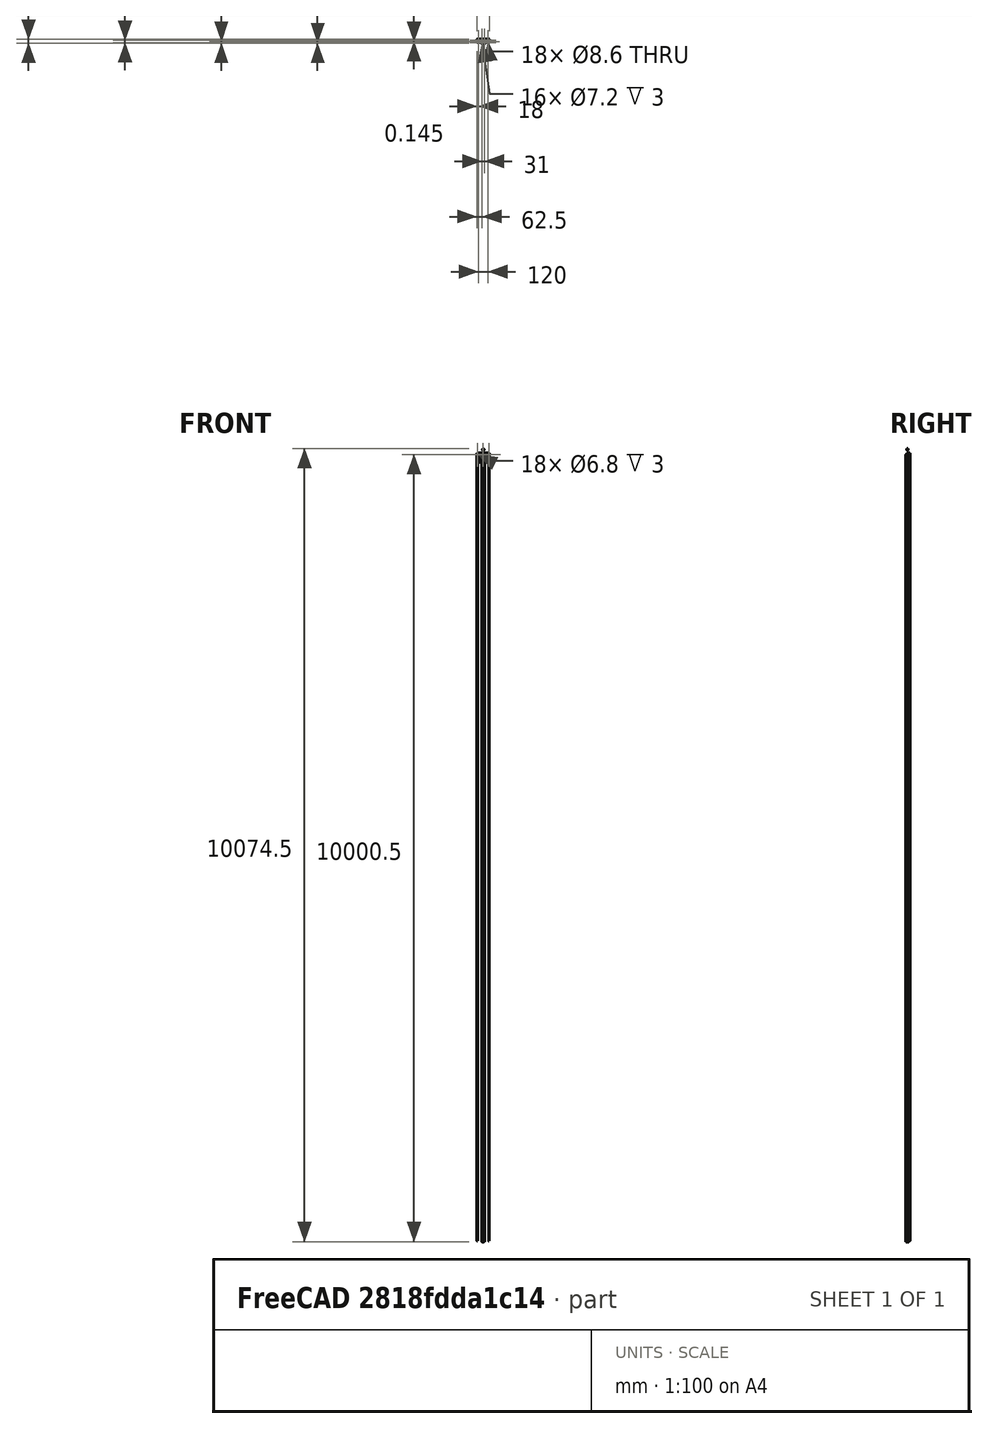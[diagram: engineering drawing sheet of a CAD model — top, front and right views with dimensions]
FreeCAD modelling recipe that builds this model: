
FCSTD DOCUMENT  (FreeCAD 0.15R4671 (Git))
Label: ZRodHolderMiddle
License: All rights reserved
LicenseURL: http://en.wikipedia.org/wiki/All_rights_reserved
objects: Sketcher::SketchObject×13, PartDesign::Pocket×10, PartDesign::Fillet×7, Part::Feature×4, PartDesign::Pad×3, PartDesign::Chamfer×2, Mesh::Feature×2
note: 52 computed .brp shape members not serialized (recipe doc carries the construction recipe); baked Part::Feature solids carry a one-line shape summary decoded from their .brp

FEATURE [Part::Feature] Part__Feature  label="TempZMotorEnd"
  shape: bbox 155 x 49.5 x 115 mm, 106 faces (baked)
FEATURE [Part::Feature] _mmBrasNut  label="8mmBrassNut"
  Placement = pos=(0,-28.14,59) rot=(0.707107,0,0.707107;3.14159rad)
  shape: bbox 22 x 22 x 16.42 mm, 29 faces (baked)
FEATURE [Sketcher::SketchObject] Sketch
  Placement = pos=(0,0,0) rot=(1,0,0;1.5708rad)
  sketch-geometry (4):
    g0: LineSegment StartX=-78 StartY=7.5 StartZ=0 EndX=78 EndY=7.5 EndZ=0
    g1: LineSegment StartX=78 StartY=7.5 StartZ=0 EndX=78 EndY=-7.5 EndZ=0
    g2: LineSegment StartX=78 StartY=-7.5 StartZ=0 EndX=-78 EndY=-7.5 EndZ=0
    g3: LineSegment StartX=-78 StartY=-7.5 StartZ=0 EndX=-78 EndY=7.5 EndZ=0
  constraints (12):
    c: Coincident(g0,g1)
    c: Coincident(g1,g2)
    c: Coincident(g2,g3)
    c: Coincident(g3,g0)
    c: Horizontal(g0)
    c: Horizontal(g2)
    c: Vertical(g1)
    c: Vertical(g3)
    c: DistanceY(g1,g0) = 15
    c: DistanceY(g-1,g1) = -7.5
    c: DistanceX(g1,g2) = -156
    c: DistanceX(g-1,g2) = -78
FEATURE [PartDesign::Pad] Pad
  Length = 36
  Length2 = 100
  Placement = pos=(0,0,0) rot=(1,0,0;1.5708rad)
  Sketch = -> Sketch
  Type = 0
FEATURE [Sketcher::SketchObject] Sketch001
  Placement = pos=(0,0,7.5) rot=(0,0,1;3.14159rad)
  Support = -> Pad [Face1]
  sketch-geometry (16):
    g0: LineSegment StartX=-80 StartY=7 StartZ=0 EndX=-68 EndY=7 EndZ=0
    g1: LineSegment StartX=-68 StartY=7 StartZ=0 EndX=-68 EndY=37 EndZ=0
    g2: LineSegment StartX=-68 StartY=37 StartZ=0 EndX=-52 EndY=37 EndZ=0
    g3: LineSegment StartX=-52 StartY=37 StartZ=0 EndX=-52 EndY=28 EndZ=0
    g4: LineSegment StartX=-52 StartY=28 StartZ=0 EndX=-32 EndY=7 EndZ=0
    g5: LineSegment StartX=-32 StartY=7 StartZ=0 EndX=32 EndY=7 EndZ=0
    g6: LineSegment StartX=32 StartY=7 StartZ=0 EndX=52 EndY=28 EndZ=0
    g7: LineSegment StartX=52 StartY=28 StartZ=0 EndX=52 EndY=37 EndZ=0
    g8: LineSegment StartX=52 StartY=37 StartZ=0 EndX=68 EndY=37 EndZ=0
    g9: LineSegment StartX=68 StartY=37 StartZ=0 EndX=68 EndY=7 EndZ=0
    g10: LineSegment StartX=68 StartY=7 StartZ=0 EndX=80 EndY=7 EndZ=0
    g11: LineSegment StartX=80 StartY=7 StartZ=0 EndX=80 EndY=53.5948 EndZ=0
    g12: LineSegment StartX=80 StartY=53.5948 StartZ=0 EndX=-80 EndY=53.5948 EndZ=0
    g13: LineSegment StartX=-80 StartY=53.5948 StartZ=0 EndX=-80 EndY=7 EndZ=0
    g14: Circle CenterX=-60 CenterY=28 CenterZ=0 NormalX=0 NormalY=0 NormalZ=1 Radius=4.3
    g15: Circle CenterX=60 CenterY=28 CenterZ=0 NormalX=0 NormalY=0 NormalZ=1 Radius=4.3
  constraints (27):
    c: Coincident(g0,g1)
    c: Coincident(g1,g2)
    c: Coincident(g2,g3)
    c: Coincident(g3,g4)
    c: Coincident(g4,g5)
    c: Coincident(g5,g6)
    c: Coincident(g6,g7)
    c: Coincident(g7,g8)
    c: Coincident(g8,g9)
    c: Coincident(g9,g10)
    c: Coincident(g10,g11)
    c: Coincident(g11,g12)
    c: Coincident(g12,g13)
    c: Coincident(g13,g0)
    c: Horizontal(g12)
    c: Vertical(g11)
    c: Vertical(g13)
    c: Vertical(g9)
    c: Vertical(g7)
    c: Vertical(g3)
    c: Vertical(g1)
    c: Horizontal(g2)
    c: Horizontal(g8)
    c: Horizontal(g10)
    c: Horizontal(g0)
    c: Radius(g15) = 4.3
    c: Equal(g15,g14)
FEATURE [PartDesign::Pocket] Pocket
  Length = 5
  Placement = pos=(0,0,0) rot=(1,0,0;1.5708rad)
  Sketch = -> Sketch001
  Type = 1
FEATURE [PartDesign::Chamfer] Chamfer
  Base = -> Pocket [Edge24,Edge27,Edge36,Edge39]
  Placement = pos=(0,0,0) rot=(1,0,0;1.5708rad)
  Size = 4
FEATURE [PartDesign::Fillet] Fillet
  Base = -> Chamfer [Edge21,Edge24,Edge28,Edge33,Edge52,Edge54,Edge51,Edge46]
  Placement = pos=(0,0,0) rot=(1,0,0;1.5708rad)
  Radius = 2
FEATURE [PartDesign::Fillet] Fillet001
  Base = -> Fillet [Edge72,Edge68,Edge64,Edge60,Edge30,Edge51]
  Placement = pos=(0,0,0) rot=(1,0,0;1.5708rad)
  Radius = 2
FEATURE [Sketcher::SketchObject] Sketch002
  Placement = pos=(0,-7,0) rot=(1,0,0;1.5708rad)
  Support = -> Fillet001 [Face26]
  sketch-geometry (3):
    g0: Circle CenterX=0 CenterY=0 CenterZ=0 NormalX=0 NormalY=0 NormalZ=1 Radius=1.8
    g1: Circle CenterX=74 CenterY=0 CenterZ=0 NormalX=0 NormalY=0 NormalZ=1 Radius=1.8
    g2: Circle CenterX=-74 CenterY=0 CenterZ=0 NormalX=0 NormalY=0 NormalZ=1 Radius=1.8
  constraints (3):
    c: Radius(g2) = 1.8
    c: Equal(g2,g0)
    c: Equal(g2,g1)
FEATURE [PartDesign::Pocket] Pocket001
  Length = 5
  Placement = pos=(0,0,0) rot=(1,0,0;1.5708rad)
  Sketch = -> Sketch002
  Type = 1
FEATURE [Sketcher::SketchObject] Sketch003
  Placement = pos=(0,-7,0) rot=(1,0,0;1.5708rad)
  Support = -> Pocket001 [Face26]
  sketch-geometry (3):
    g0: Circle CenterX=0 CenterY=0 CenterZ=0 NormalX=0 NormalY=0 NormalZ=1 Radius=3.4
    g1: Circle CenterX=74 CenterY=0 CenterZ=0 NormalX=0 NormalY=0 NormalZ=1 Radius=3.4
    g2: Circle CenterX=-74 CenterY=0 CenterZ=0 NormalX=0 NormalY=0 NormalZ=1 Radius=3.4
  constraints (3):
    c: Radius(g2) = 3.4
    c: Equal(g2,g0)
    c: Equal(g2,g1)
FEATURE [PartDesign::Pocket] Pocket002
  Length = 3
  Placement = pos=(0,0,0) rot=(1,0,0;1.5708rad)
  Sketch = -> Sketch003
  Type = 0
FEATURE [PartDesign::Fillet] Fillet002
  Base = -> Pocket002 [Edge59,Edge10,Edge48,Edge6]
  Placement = pos=(0,0,0) rot=(1,0,0;1.5708rad)
  Radius = 4
FEATURE [Mesh::Feature] MicroSwitch
  Placement = pos=(68.3,-20,3) rot=(0.57735,0.57735,0.57735;2.0944rad)
FEATURE [Sketcher::SketchObject] Sketch004
  Placement = pos=(68,0,0) rot=(0.707107,0,0.707107;3.14159rad)
  Support = -> Fillet002 [Face6]
  sketch-geometry (2):
    g0: Circle CenterX=0.25 CenterY=24.5 CenterZ=0 NormalX=0 NormalY=0 NormalZ=1 Radius=1
    g1: Circle CenterX=0.25 CenterY=15 CenterZ=0 NormalX=0 NormalY=0 NormalZ=1 Radius=1
  constraints (2):
    c: Radius(g1) = 1
    c: Equal(g1,g0)
FEATURE [PartDesign::Pocket] Pocket003  label="ZRodHolderMiddle_1"
  Length = 4
  Placement = pos=(0,0,0) rot=(1,0,0;1.5708rad)
  Sketch = -> Sketch004
  Type = 0
FEATURE [PartDesign::Fillet] Fillet003
  Base = -> Pocket003 [Edge26]
  Placement = pos=(0,0,0) rot=(1,0,0;1.5708rad)
  Radius = 1
FEATURE [Part::Feature] Fillet004  label="ZRodHolderMiddle_2"
  shape: bbox 156.7 x 36 x 15.66 mm, 122 faces (baked)
FEATURE [Sketcher::SketchObject] Sketch005
  Placement = pos=(0,0,7.5) rot=(0,0,1;0rad)
  Support = -> Fillet004 [Face1]
  sketch-geometry (8):
    g0: LineSegment StartX=65 StartY=-6 StartZ=0 EndX=36 EndY=-6 EndZ=0
    g1: LineSegment StartX=36 StartY=-6 StartZ=0 EndX=51 EndY=-21 EndZ=0
    g2: LineSegment StartX=51 StartY=-21 StartZ=0 EndX=65 EndY=-21 EndZ=0
    g3: LineSegment StartX=65 StartY=-21 StartZ=0 EndX=65 EndY=-6 EndZ=0
    g4: LineSegment StartX=-37 StartY=-7 StartZ=0 EndX=-65 EndY=-7 EndZ=0
    g5: LineSegment StartX=-65 StartY=-7 StartZ=0 EndX=-65 EndY=-21 EndZ=0
    g6: LineSegment StartX=-65 StartY=-21 StartZ=0 EndX=-51 EndY=-21 EndZ=0
    g7: LineSegment StartX=-51 StartY=-21 StartZ=0 EndX=-37 EndY=-7 EndZ=0
  constraints (8):
    c: Coincident(g0,g1)
    c: Coincident(g1,g2)
    c: Coincident(g2,g3)
    c: Coincident(g3,g0)
    c: Coincident(g4,g5)
    c: Coincident(g5,g6)
    c: Coincident(g6,g7)
    c: Coincident(g7,g4)
FEATURE [PartDesign::Pocket] Pocket004
  Length = 12
  Sketch = -> Sketch005
  Type = 0
FEATURE [PartDesign::Fillet] Fillet005
  Base = -> Pocket004 [Edge128,Edge134,Edge132,Edge130,Edge118,Edge120,Edge122,Edge124]
  Radius = 2
FEATURE [PartDesign::Fillet] Fillet006  label="ZRodHolderMiddle"
  Base = -> Fillet005 [Edge6,Edge45]
  Radius = 1
FEATURE [Sketcher::SketchObject] Sketch006
  Placement = pos=(0,0,-7.5) rot=(1,0,0;3.14159rad)
  Support = -> Fillet006 [Face66]
  sketch-geometry (4):
    g0: LineSegment StartX=-27 StartY=4.78307 StartZ=0 EndX=27 EndY=4.78307 EndZ=0
    g1: LineSegment StartX=27 StartY=4.78307 StartZ=0 EndX=27 EndY=50 EndZ=0
    g2: LineSegment StartX=27 StartY=50 StartZ=0 EndX=-27 EndY=50 EndZ=0
    g3: LineSegment StartX=-27 StartY=50 StartZ=0 EndX=-27 EndY=4.78307 EndZ=0
  constraints (8):
    c: Coincident(g0,g1)
    c: Coincident(g1,g2)
    c: Coincident(g2,g3)
    c: Coincident(g3,g0)
    c: Horizontal(g0)
    c: Horizontal(g2)
    c: Vertical(g1)
    c: Vertical(g3)
FEATURE [Part::Feature] Part__Feature001  label="NEMA_17"
  Placement = pos=(0,-28.14,-7.7) rot=(0,0,1;3.14159rad)
  shape: bbox 42.3 x 42.3 x 68 mm, 275 faces (baked)
FEATURE [Mesh::Feature] acoplador_flexivel  label="5x8mmFlexCoupler"
  Placement = pos=(0,-28.14,26) rot=(1,0,0;3.14159rad)
FEATURE [PartDesign::Pad] Pad001
  Length = 7
  Length2 = 100
  Reversed = true
  Sketch = -> Sketch006
  Type = 0
FEATURE [Sketcher::SketchObject] Sketch007
  Placement = pos=(0,-4.78307,0) rot=(0,0.707107,0.707107;3.14159rad)
  Support = -> Pad001 [Face22]
  sketch-geometry (1):
    g0: Circle CenterX=0 CenterY=0 CenterZ=0 NormalX=0 NormalY=0 NormalZ=1 Radius=1.81
  constraints (1):
    c: Radius(g0) = 1.81
FEATURE [PartDesign::Pocket] Pocket005
  Length = 8
  Sketch = -> Sketch007
  Type = 0
FEATURE [Sketcher::SketchObject] Sketch008
  Placement = pos=(0,-12.7831,0) rot=(0,0.707107,0.707107;3.14159rad)
  Support = -> Pocket005 [Face92]
  sketch-geometry (1):
    g0: Circle CenterX=0 CenterY=0 CenterZ=0 NormalX=0 NormalY=0 NormalZ=1 Radius=3.6
  constraints (1):
    c: Radius(g0) = 3.6
FEATURE [PartDesign::Pocket] Pocket006
  Length = 9
  Reversed = true
  Sketch = -> Sketch008
  Type = 0
FEATURE [Sketcher::SketchObject] Sketch009
  Placement = pos=(0,0,-0.5) rot=(0,0,1;0rad)
  Support = -> Pocket006 [Face51]
  sketch-geometry (5):
    g0: Circle CenterX=-15.5 CenterY=-12.6481 CenterZ=0 NormalX=0 NormalY=0 NormalZ=1 Radius=1.8
    g1: Circle CenterX=15.5 CenterY=-12.6643 CenterZ=0 NormalX=0 NormalY=0 NormalZ=1 Radius=1.8
    g2: Circle CenterX=15.5 CenterY=-43.6492 CenterZ=0 NormalX=0 NormalY=0 NormalZ=1 Radius=1.8
    g3: Circle CenterX=-15.5 CenterY=-43.6486 CenterZ=0 NormalX=0 NormalY=0 NormalZ=1 Radius=1.8
    g4: Circle CenterX=0 CenterY=-28.25 CenterZ=0 NormalX=0 NormalY=0 NormalZ=1 Radius=12
  constraints (5):
    c: Radius(g4) = 12
    c: Radius(g3) = 1.8
    c: Equal(g3,g0)
    c: Equal(g3,g1)
    c: Equal(g3,g2)
FEATURE [PartDesign::Pocket] Pocket007
  Length = 5
  Sketch = -> Sketch009
  Type = 1
FEATURE [Sketcher::SketchObject] Sketch010
  Placement = pos=(0,0,-0.5) rot=(0,0,1;0rad)
  Support = -> Pocket007 [Face56]
  sketch-geometry (4):
    g0: Circle CenterX=-15.5 CenterY=-43.6508 CenterZ=0 NormalX=0 NormalY=0 NormalZ=1 Radius=3.6
    g1: Circle CenterX=15.5 CenterY=-43.6458 CenterZ=0 NormalX=0 NormalY=0 NormalZ=1 Radius=3.6
    g2: Circle CenterX=15.5 CenterY=-12.6561 CenterZ=0 NormalX=0 NormalY=0 NormalZ=1 Radius=3.6
    g3: Circle CenterX=-15.5 CenterY=-12.6528 CenterZ=0 NormalX=0 NormalY=0 NormalZ=1 Radius=3.6
  constraints (4):
    c: Radius(g3) = 3.6
    c: Equal(g3,g2)
    c: Equal(g3,g1)
    c: Equal(g3,g0)
FEATURE [PartDesign::Pocket] Pocket008
  Length = 3
  Sketch = -> Sketch010
  Type = 0
FEATURE [PartDesign::Chamfer] Chamfer001
  Base = -> Pocket008 [Edge67,Edge66]
  Size = 8
FEATURE [Sketcher::SketchObject] Sketch011
  Placement = pos=(0,0,-0.5) rot=(0,0,1;0rad)
  Support = -> Chamfer001 [Face47]
  sketch-geometry (8):
    g0: LineSegment StartX=-27 StartY=-5.5 StartZ=0 EndX=-24 EndY=-5.5 EndZ=0
    g1: LineSegment StartX=-24 StartY=-5.5 StartZ=0 EndX=-24 EndY=-42 EndZ=0
    g2: LineSegment StartX=-24 StartY=-42 StartZ=0 EndX=-27 EndY=-42 EndZ=0
    g3: LineSegment StartX=-27 StartY=-42 StartZ=0 EndX=-27 EndY=-5.5 EndZ=0
    g4: LineSegment StartX=27 StartY=-5.37655 StartZ=0 EndX=24 EndY=-5.37655 EndZ=0
    g5: LineSegment StartX=24 StartY=-5.37655 StartZ=0 EndX=24 EndY=-42 EndZ=0
    g6: LineSegment StartX=24 StartY=-42 StartZ=0 EndX=27 EndY=-42 EndZ=0
    g7: LineSegment StartX=27 StartY=-42 StartZ=0 EndX=27 EndY=-5.37655 EndZ=0
  constraints (16):
    c: Coincident(g0,g1)
    c: Coincident(g1,g2)
    c: Coincident(g2,g3)
    c: Coincident(g3,g0)
    c: Horizontal(g0)
    c: Horizontal(g2)
    c: Vertical(g1)
    c: Vertical(g3)
    c: Coincident(g4,g5)
    c: Coincident(g5,g6)
    c: Coincident(g6,g7)
    c: Coincident(g7,g4)
    c: Horizontal(g4)
    c: Horizontal(g6)
    c: Vertical(g5)
    c: Vertical(g7)
FEATURE [PartDesign::Pad] Pad002
  Length = 8
  Length2 = 100
  Sketch = -> Sketch011
  Type = 0
FEATURE [Sketcher::SketchObject] Sketch012
  Placement = pos=(27,0,0) rot=(0.57735,0.57735,0.57735;2.0944rad)
  Support = -> Pad002 [Face166]
  sketch-geometry (5):
    g0: LineSegment StartX=-43 StartY=-0.5 StartZ=0 EndX=-42 EndY=-0.5 EndZ=0
    g1: LineSegment StartX=-42 StartY=-0.5 StartZ=0 EndX=-6 EndY=7.5 EndZ=0
    g2: LineSegment StartX=-6 StartY=7.5 StartZ=0 EndX=-6 EndY=8.5 EndZ=0
    g3: LineSegment StartX=-6 StartY=8.5 StartZ=0 EndX=-43 EndY=8.5 EndZ=0
    g4: LineSegment StartX=-43 StartY=8.5 StartZ=0 EndX=-43 EndY=-0.5 EndZ=0
  constraints (5):
    c: Coincident(g0,g1)
    c: Coincident(g1,g2)
    c: Coincident(g2,g3)
    c: Coincident(g3,g4)
    c: Coincident(g4,g0)
FEATURE [PartDesign::Pocket] Pocket009  label="ZRodHolderMotor"
  Length = 54
  Sketch = -> Sketch012
  Type = 0
FEATURE [PartDesign::Fillet] Fillet007  label="ZRodHolderMiddle001"
  Base = -> Pocket009 [Edge308,Edge390,Edge386,Edge306]
  Radius = 2
